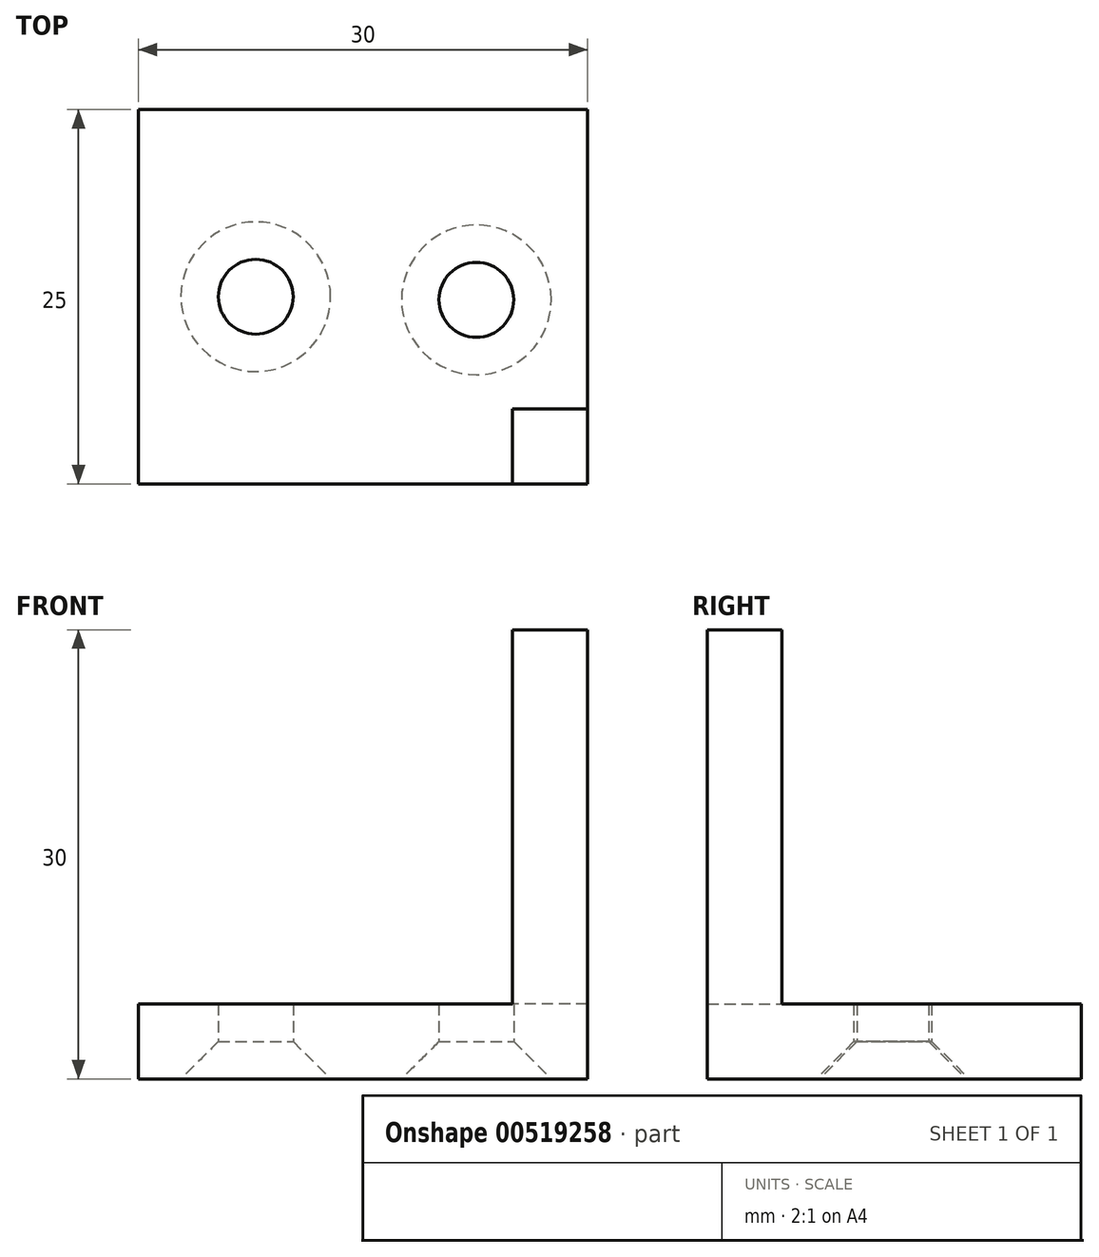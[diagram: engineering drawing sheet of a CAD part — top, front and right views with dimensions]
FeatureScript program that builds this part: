
annotation { "Feature Type Name" : "Feature", "Feature Type Description" : "" }
export const myFeature = defineFeature(function(context is Context, id is Id, definition is map)
    precondition{}
    {
        {
            var Q0;
            Q0=qCreatedBy(makeId("Top.planeOp"),FACE);
            var sketch = newSketch(context, id + "F0", { "sketchPlane" : qUnion([Q0])});
            skLineSegment(sketch, "E0.bottom", {"start": v(15, 12.5) * mm, "end": v(-15, 12.5) * mm});
            skLineSegment(sketch, "E0.top", {"start": v(15, -12.5) * mm, "end": v(-15, -12.5) * mm});
            skLineSegment(sketch, "E0.left", {"start": v(15, 12.5) * mm, "end": v(15, -12.5) * mm});
            skLineSegment(sketch, "E0.right", {"start": v(-15, 12.5) * mm, "end": v(-15, -12.5) * mm});
            skPoint(sketch, "E0.middle", {"position": v(0, 0) * mm});
            skSolve(sketch);
        }
        {
            var Q0;
            Q0 = qSketchRegion(id + "F0", true);
            extrude(context, id + "F1", {"entities" : qUnion([Q0]), "depth" : 5 * mm, "offsetDistance" : 25 * mm});
        }
        {
            var Q0;
            Q0=makeQuery(id+"F1.opExtrude","CAP_FACE",FACE,{"disambiguationData":[OSD([sQuery(id+"F0.wireOp",EDGE,"E0.bottom"),sQuery(id+"F0.wireOp",EDGE,"E0.top"),sQuery(id+"F0.wireOp",EDGE,"E0.left"),sQuery(id+"F0.wireOp",EDGE,"E0.right")])],"isStart":false});
            var sketch = newSketch(context, id + "F2", { "sketchPlane" : qUnion([Q0])});
            skLineSegment(sketch, "E1.bottom", {"start": v(15, -12.5) * mm, "end": v(10, -12.5) * mm});
            skLineSegment(sketch, "E1.top", {"start": v(15, -7.5) * mm, "end": v(10, -7.5) * mm});
            skLineSegment(sketch, "E1.left", {"start": v(15, -12.5) * mm, "end": v(15, -7.5) * mm});
            skLineSegment(sketch, "E1.right", {"start": v(10, -12.5) * mm, "end": v(10, -7.5) * mm});
            skSolve(sketch);
        }
        {
            var Q0;
            Q0 = qSketchRegion(id + "F2", true);
            extrude(context, id + "F3", {"entities" : qUnion([Q0]), "operationType" : NewBodyOperationType.ADD, "depth" : 25 * mm, "offsetDistance" : 25 * mm});
        }
        {
            var Q0;
            Q0=makeQuery(id+"F1.opExtrude","CAP_FACE",FACE,{"disambiguationData":[OSD([sQuery(id+"F0.wireOp",EDGE,"E0.bottom"),sQuery(id+"F0.wireOp",EDGE,"E0.top"),sQuery(id+"F0.wireOp",EDGE,"E0.left"),sQuery(id+"F0.wireOp",EDGE,"E0.right")])],"isStart":true});
            var sketch = newSketch(context, id + "F4", { "sketchPlane" : qUnion([Q0])});
            skPoint(sketch, "E2", {"position": v(-7.16, 0) * mm});
            skPoint(sketch, "E3", {"position": v(7.58, 0.2) * mm});
            skSolve(sketch);
        }
        {
            var Q0;
            Q0=sQuery(id+"F4.wireOp",VERTEX,"E2");
            var Q1;
            Q1=sQuery(id+"F4.wireOp",VERTEX,"E3");
            var Q2;
            Q2=makeQuery(id+"F1.opExtrude","SWEPT_BODY",BODY,{"disambiguationData":[OSD([sQuery(id+"F0.wireOp",EDGE,"E0.bottom"),sQuery(id+"F0.wireOp",EDGE,"E0.top"),sQuery(id+"F0.wireOp",EDGE,"E0.left"),sQuery(id+"F0.wireOp",EDGE,"E0.right")])]});
            var Q3;
            Q3=makeQuery(id+"F5MkpdqGYMDcvco_1.1.F1.opExtrude","SWEPT_BODY",BODY,{"disambiguationData":[OSD([sQuery(id+"F0.wireOp",EDGE,"E0.bottom"),sQuery(id+"F0.wireOp",EDGE,"E0.top"),sQuery(id+"F0.wireOp",EDGE,"E0.left"),sQuery(id+"F0.wireOp",EDGE,"E0.right")])]});
            var Q4;
            Q4=makeQuery(id+"FOlUxba3fGox4B5_2.1.F5MkpdqGYMDcvco_1.1.F1.opExtrude","SWEPT_BODY",BODY,{"disambiguationData":[OSD([sQuery(id+"F0.wireOp",EDGE,"E0.bottom"),sQuery(id+"F0.wireOp",EDGE,"E0.top"),sQuery(id+"F0.wireOp",EDGE,"E0.left"),sQuery(id+"F0.wireOp",EDGE,"E0.right")])]});
            hole(context, id + "F5", {"style" : HoleStyle.C_SINK, "endStyle" : HoleEndStyle.THROUGH, "holeDiameter" : 5 * mm, "cSinkDiameter" : 10 * mm, "cSinkAngle" : 90 * degree, "isTappedThrough" : true, "tappedDepth" : 12 * mm, "tapClearance" : 3, "startFromSketch" : true, "locations" : qUnion([Q0, Q1]), "scope" : qUnion([Q2, Q3, Q4])});
        }
    });
